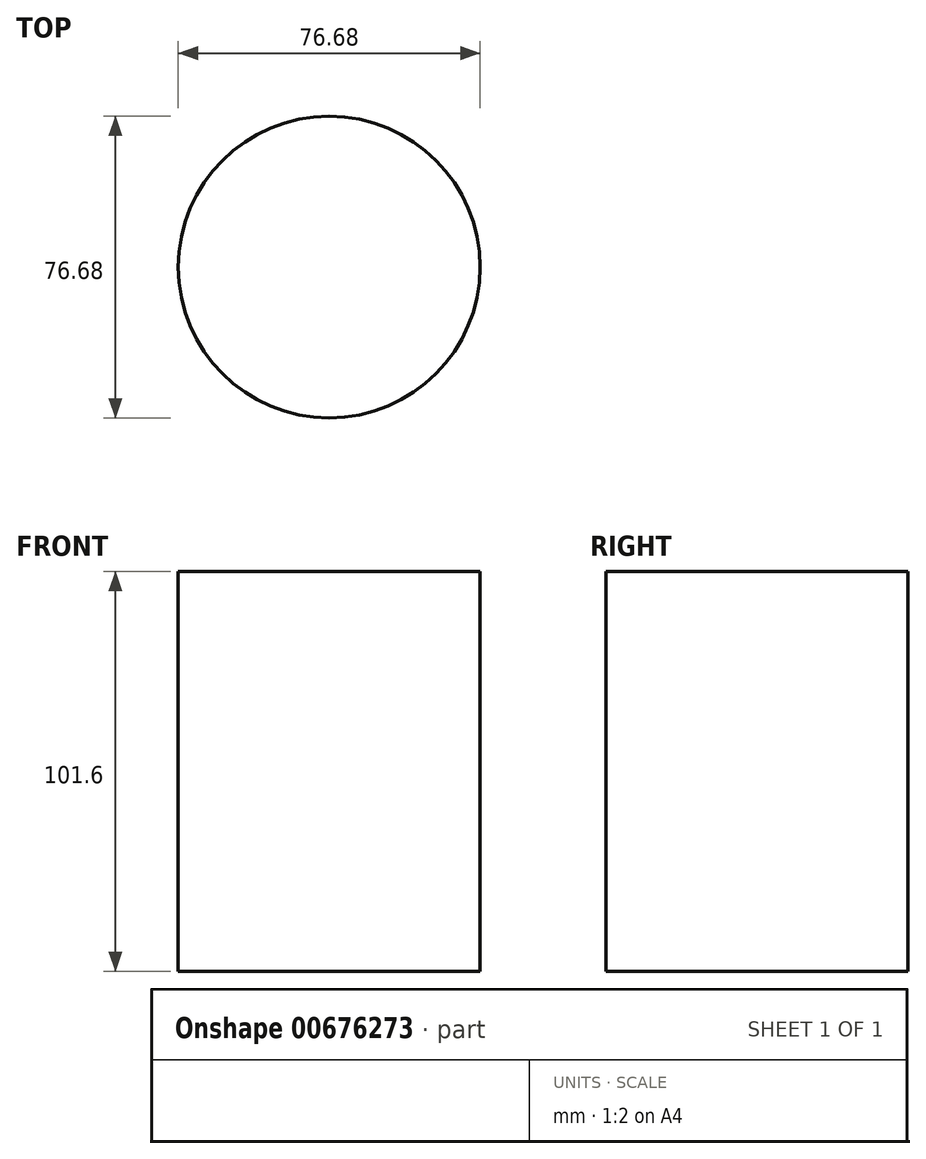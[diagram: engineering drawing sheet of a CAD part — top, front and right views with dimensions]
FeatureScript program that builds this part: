
annotation { "Feature Type Name" : "Feature", "Feature Type Description" : "" }
export const myFeature = defineFeature(function(context is Context, id is Id, definition is map)
    precondition{}
    {
        {
            var Q0;
            Q0=qCreatedBy(makeId("Top.planeOp"),FACE);
            var sketch = newSketch(context, id + "F0", { "sketchPlane" : qUnion([Q0])});
            skCircle(sketch, "E0", {"center": v(0, 0) * mm, "radius": 38.34 * mm});
            skSolve(sketch);
        }
        {
            var Q0;
            Q0=makeQuery(id+"F0.imprint","IMPRINT",FACE,{"disambiguationData":[TD([[makeQuery(id+"F0.imprint","IMPRINT",EDGE,{"derivedFrom":sQuery(id+"F0.wireOp",EDGE,"E0")}),1.0]])]});
            extrude(context, id + "F1", {"entities" : qUnion([Q0]), "depth" : 101.6 * mm, "offsetDistance" : 25.4 * mm});
        }
    });
